# Revit family: Trane_TVR_Indoor_4-way Cassette_4TVC0055EF000AA (2nd DC) - 360°
name_source: partatom
category: Equipamento mecânico
units: mm (PartAtom-declared; Revit-internal decimal feet)

## family parameters
Com base no plano de trabalho = Não
Compartilhado = Não
Corte com vazios quando carregada = Não
Cota do conector redondo = Utilizar diâmetro
Número OmniClass = 23.75.00.00
Ponto de cálculo do ambiente = Não
Sempre na vertical = Sim
Tipo de parte = Normal
Título OmniClass = Climate Control (HVAC)

## types (1)
- 4TVC0055EF000AA
    Air Flow = 2100/1950/1800/1750/1600/1450/1350
    Condensation = air
    Cooling Capacity = 16.00 kW
    Cooling Power Input = 170 W
    Depth = 950  [stored 3.1168 ft]
    Descrição = High efficiency air cooled
    Drain pipe = 32  [stored 0.104987 ft]
    Fabricante = TRANE
    Gas = R410a
    Gas pipe = 15.9  [stored 0.0521654 ft]
    Gross Weight = 35.30 kg
    Heating Capacity = 18.00 kW
    Heating Power Input = 170 W
    Height = 300
    Installation = Indoor installation
    Liquid pipe = 9.53
    Machine material = grilles：ABS/HIPS
    Maximum Fuse Amps = 15 A
    Minimum Circuit Amps = 1 A
    Modelo = 4TVC0055EF000AA
    Panel color = S1004
    Power supply = 1 phase, 220-240V, 50/60Hz
    Series = ULTRA
    URL = https://www.trane.com
    Width = 950  [stored 3.1168 ft]
    clearance access behind = 1000  [stored 3.28084 ft]
    clearance access front = 1000  [stored 3.28084 ft]
    clearance access left = 1000  [stored 3.28084 ft]
    clearance access right = 1000  [stored 3.28084 ft]

note: [stored X ft] marks values corroborated as IEEE doubles in the binary element streams (Revit-internal decimal feet)

## geometry (parser evidence)
native form markers: Blend x2, Sweep x5
no freeform markers — native parametric forms only
